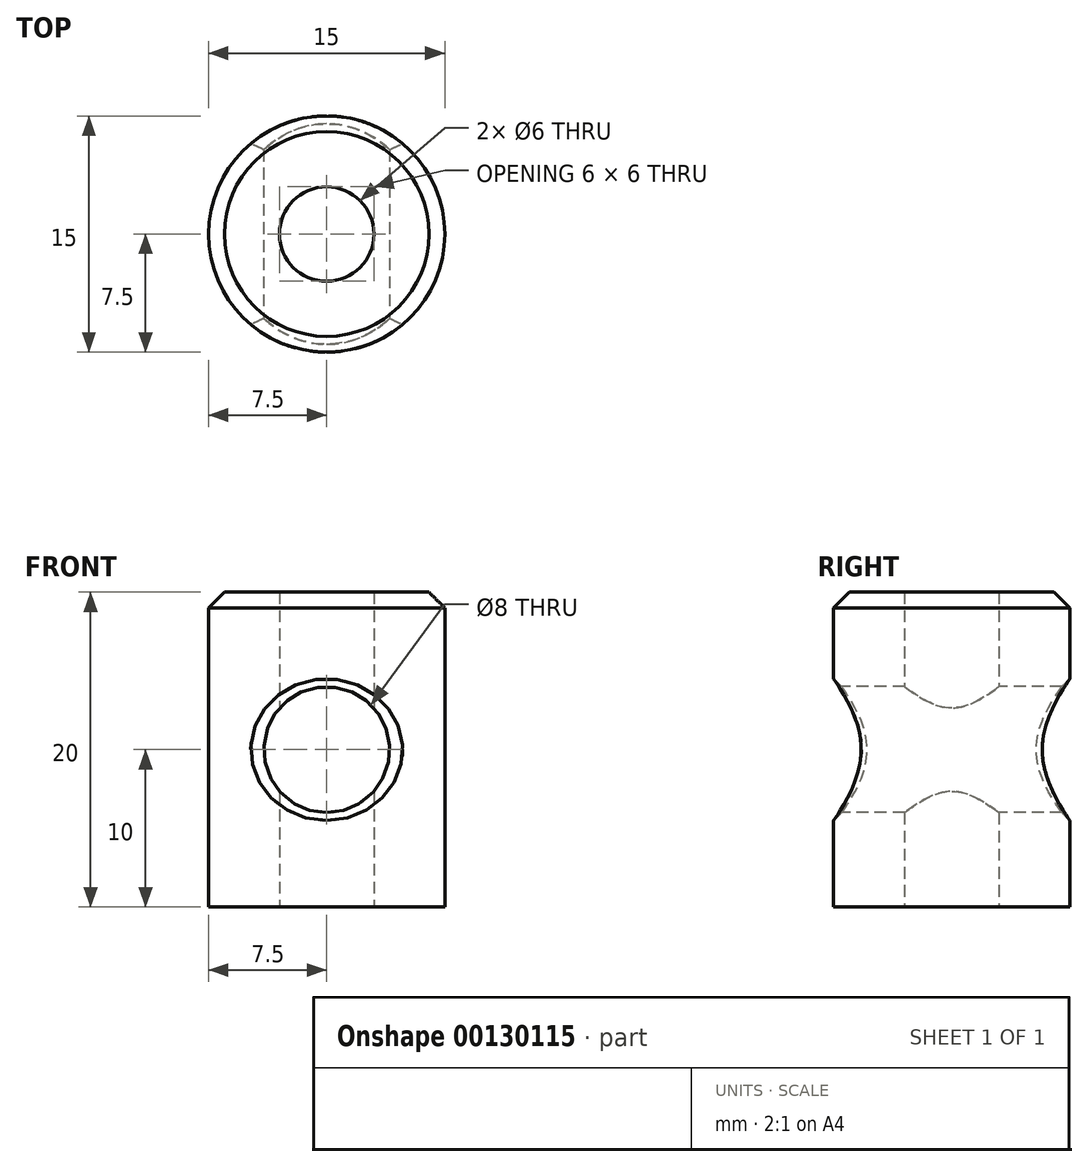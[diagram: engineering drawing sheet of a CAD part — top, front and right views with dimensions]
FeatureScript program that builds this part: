
annotation { "Feature Type Name" : "Feature", "Feature Type Description" : "" }
export const myFeature = defineFeature(function(context is Context, id is Id, definition is map)
    precondition{}
    {
        {
            var Q0;
            Q0=qCreatedBy(makeId("Top.planeOp"),FACE);
            var sketch = newSketch(context, id + "F0", { "sketchPlane" : qUnion([Q0])});
            skCircle(sketch, "E0", {"center": v(0, 0) * mm, "radius": 7.5 * mm});
            skCircle(sketch, "E1", {"center": v(0, 0) * mm, "radius": 3 * mm});
            skSolve(sketch);
        }
        {
            var Q0;
            Q0=makeQuery(id+"F0.imprint","IMPRINT",FACE,{"disambiguationData":[TD([[makeQuery(id+"F0.imprint","IMPRINT",EDGE,{"derivedFrom":sQuery(id+"F0.wireOp",EDGE,"E0")}),1.0]])]});
            extrude(context, id + "F1", {"entities" : qUnion([Q0]), "depth" : 20 * mm, "symmetric" : true});
        }
        {
            var Q0;
            Q0=qCreatedBy(makeId("Front.planeOp"),FACE);
            var sketch = newSketch(context, id + "F2", { "sketchPlane" : qUnion([Q0])});
            skCircle(sketch, "E2", {"center": v(0, 0) * mm, "radius": 4 * mm});
            skSolve(sketch);
        }
        {
            var Q0;
            Q0=makeQuery(id+"F2.imprint","IMPRINT",FACE,{"disambiguationData":[TD([[makeQuery(id+"F2.imprint","IMPRINT",EDGE,{"derivedFrom":sQuery(id+"F2.wireOp",EDGE,"E2")}),1.0]])]});
            extrude(context, id + "F3", {"entities" : qUnion([Q0]), "operationType" : NewBodyOperationType.REMOVE, "oppositeDirection" : true, "depth" : 25 * mm, "symmetric" : true});
        }
        {
            var Q0;
            Q0=makeQuery(id+"F1.opExtrude","CAP_EDGE",EDGE,{"disambiguationData":[OSD([sQuery(id+"F0.wireOp",EDGE,"E0")])],"isStart":false});
            chamfer(context, id + "F4", {"entities" : qUnion([Q0]), "width" : 1 * mm, "tangentPropagation" : true});
        }
        {
            var Q0;
            Q0=makeQuery(id+"F3.boolean.opBoolean","INTERSECT",EDGE,{"disambiguationData":[OD(0.0)],"derivedFrom":[makeQuery(id+"F1.opExtrude","SWEPT_FACE",FACE,{"disambiguationData":[OSD([sQuery(id+"F0.wireOp",EDGE,"E0")])]}),makeQuery(id+"F3.opExtrude","SWEPT_FACE",FACE,{"disambiguationData":[OSD([sQuery(id+"F2.wireOp",EDGE,"E2")])]})]});
            var Q1;
            Q1=makeQuery(id+"F3.boolean.opBoolean","INTERSECT",EDGE,{"disambiguationData":[OD(1.0)],"derivedFrom":[makeQuery(id+"F1.opExtrude","SWEPT_FACE",FACE,{"disambiguationData":[OSD([sQuery(id+"F0.wireOp",EDGE,"E0")])]}),makeQuery(id+"F3.opExtrude","SWEPT_FACE",FACE,{"disambiguationData":[OSD([sQuery(id+"F2.wireOp",EDGE,"E2")])]})]});
            chamfer(context, id + "F5", {"entities" : qUnion([Q0, Q1]), "width" : 0.5 * mm, "tangentPropagation" : true});
        }
    });
